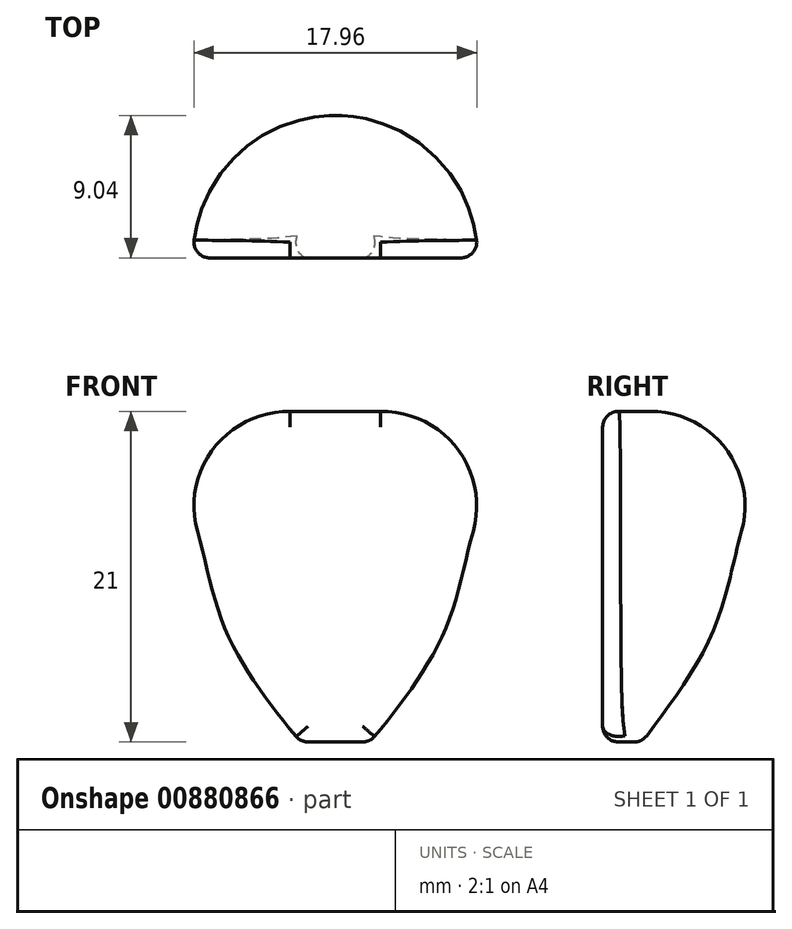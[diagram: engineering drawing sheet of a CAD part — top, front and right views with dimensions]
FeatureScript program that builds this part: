
annotation { "Feature Type Name" : "Feature", "Feature Type Description" : "" }
export const myFeature = defineFeature(function(context is Context, id is Id, definition is map)
    precondition{}
    {
        {
            var Q0;
            Q0=qCreatedBy(makeId("Top.planeOp"),FACE);
            cPlane(context, id + "F0", {"entities" : qUnion([Q0]), "cplaneType" : CPlaneType.OFFSET, "offset" : 10 * mm, "oppositeDirection" : true, "width" : 150 * mm, "height" : 150 * mm});
        }
        {
            var Q0;
            Q0=qCreatedBy(id+"F0.planeOp",FACE);
            cPlane(context, id + "F1", {"entities" : qUnion([Q0]), "cplaneType" : CPlaneType.OFFSET, "offset" : 10 * mm, "oppositeDirection" : true, "width" : 150 * mm, "height" : 150 * mm});
        }
        {
            var Q0;
            Q0=qCreatedBy(id+"F1.planeOp",FACE);
            cPlane(context, id + "F2", {"entities" : qUnion([Q0]), "cplaneType" : CPlaneType.OFFSET, "offset" : 7 * mm, "oppositeDirection" : true, "width" : 150 * mm, "height" : 150 * mm});
        }
        {
            var Q0;
            Q0=qCreatedBy(id+"F2.planeOp",FACE);
            cPlane(context, id + "F3", {"entities" : qUnion([Q0]), "cplaneType" : CPlaneType.OFFSET, "offset" : 7 * mm, "oppositeDirection" : true, "width" : 150 * mm, "height" : 150 * mm});
        }
        {
            var Q0;
            Q0=qCreatedBy(id+"F1.planeOp",FACE);
            var sketch = newSketch(context, id + "F4", { "sketchPlane" : qUnion([Q0])});
            skArc(sketch, "E0", {"start": v(12, 0) * mm, "mid": v(0, 12) * mm, "end": v(-12, 0) * mm});
            skLineSegment(sketch, "E1", {"start": v(-12, 0) * mm, "end": v(12, 0) * mm});
            skSolve(sketch);
        }
        {
            var Q0;
            Q0=qCreatedBy(id+"F3.planeOp",FACE);
            var sketch = newSketch(context, id + "F5", { "sketchPlane" : qUnion([Q0])});
            skArc(sketch, "E2", {"start": v(7, 0) * mm, "mid": v(0, 7) * mm, "end": v(-7, 0) * mm});
            skLineSegment(sketch, "E3", {"start": v(-7, 0) * mm, "end": v(7, 0) * mm});
            skSolve(sketch);
        }
        {
            var Q0;
            Q0=qCreatedBy(id+"F2.planeOp",FACE);
            var sketch = newSketch(context, id + "F6", { "sketchPlane" : qUnion([Q0])});
            skArc(sketch, "E4", {"start": v(9, 0) * mm, "mid": v(0, 9) * mm, "end": v(-9, 0) * mm});
            skLineSegment(sketch, "E5", {"start": v(-9, 0) * mm, "end": v(9, 0) * mm});
            skSolve(sketch);
        }
        {
            var Q0;
            Q0=qCreatedBy(id+"F3.planeOp",FACE);
            cPlane(context, id + "F7", {"entities" : qUnion([Q0]), "cplaneType" : CPlaneType.OFFSET, "offset" : 7 * mm, "oppositeDirection" : true, "width" : 150 * mm, "height" : 150 * mm});
        }
        {
            var Q0;
            Q0=qCreatedBy(id+"F7.planeOp",FACE);
            var sketch = newSketch(context, id + "F8", { "sketchPlane" : qUnion([Q0])});
            skArc(sketch, "E6", {"start": v(2.5, 0) * mm, "mid": v(0, 2.5) * mm, "end": v(-2.5, 0) * mm});
            skLineSegment(sketch, "E7", {"start": v(-2.5, 0) * mm, "end": v(2.5, 0) * mm});
            skSolve(sketch);
        }
        {
            var Q0;
            Q0=makeQuery(id+"F4.imprint","IMPRINT",FACE,{"disambiguationData":[TD([[makeQuery(id+"F4.imprint","IMPRINT",EDGE,{"derivedFrom":sQuery(id+"F4.wireOp",EDGE,"E0")}),1.0]])]});
            var Q1;
            Q1=makeQuery(id+"F6.imprint","IMPRINT",FACE,{"disambiguationData":[TD([[makeQuery(id+"F6.imprint","IMPRINT",EDGE,{"derivedFrom":sQuery(id+"F6.wireOp",EDGE,"E4")}),1.0]])]});
            var Q2;
            Q2=makeQuery(id+"F5.imprint","IMPRINT",FACE,{"disambiguationData":[TD([[makeQuery(id+"F5.imprint","IMPRINT",EDGE,{"derivedFrom":sQuery(id+"F5.wireOp",EDGE,"E2")}),1.0]])]});
            var Q3;
            Q3=makeQuery(id+"F8.imprint","IMPRINT",FACE,{"disambiguationData":[TD([[makeQuery(id+"F8.imprint","IMPRINT",EDGE,{"derivedFrom":sQuery(id+"F8.wireOp",EDGE,"E6")}),1.0]])]});
            loft(context, id + "F9", {"sheetProfilesArray" : [{ "sheetProfileEntities" : qUnion([Q0]) }, { "sheetProfileEntities" : qUnion([Q1]) }, { "sheetProfileEntities" : qUnion([Q2]) }, { "sheetProfileEntities" : qUnion([Q3]) }]});
        }
        {
            var Q0;
            {var subQ0=sQuery(id+"F4.wireOp",EDGE,"E0");var subQ1=sQuery(id+"F4.wireOp",EDGE,"E1");Q0=makeQuery(id+"F9.opLoft","MID_CAP_EDGE",EDGE,{"disambiguationData":[OSD([subQ0,subQ1]),TDD([makeQuery(id+"F4.imprint","INTERSECT",VERTEX,{"disambiguationData":[OD(0.0)],"derivedFrom":[subQ0,subQ1]}),makeQuery(id+"F4.imprint","INTERSECT",VERTEX,{"disambiguationData":[OD(1.0)],"derivedFrom":[subQ0,subQ1]}),makeQuery(id+"F4.imprint","IMPRINT",EDGE,{"derivedFrom":subQ0})])],"capPos":0.0});}
            fillet(context, id + "F10", {"entities" : qUnion([Q0]), "radius" : 6 * mm, "tangentPropagation" : true, "allowEdgeOverflow" : false});
        }
        {
            var Q0;
            {var subQ0=sQuery(id+"F8.wireOp",EDGE,"E7");var subQ1=sQuery(id+"F8.wireOp",EDGE,"E6");var subQ2=sQuery(id+"F6.wireOp",EDGE,"E5");var subQ3=sQuery(id+"F6.wireOp",EDGE,"E4");var subQ4=sQuery(id+"F5.wireOp",EDGE,"E3");var subQ5=sQuery(id+"F5.wireOp",EDGE,"E2");var subQ6=sQuery(id+"F4.wireOp",EDGE,"E1");var subQ7=sQuery(id+"F4.wireOp",EDGE,"E0");Q0=makeQuery(id+"F9.opLoft","SWEPT_EDGE",EDGE,{"disambiguationData":[OSD([subQ7,subQ6,subQ5,subQ4,subQ3,subQ2,subQ1,subQ0]),TDD([makeQuery(id+"F4.imprint","INTERSECT",VERTEX,{"disambiguationData":[OD(0.0)],"derivedFrom":[subQ7,subQ6]}),makeQuery(id+"F5.imprint","INTERSECT",VERTEX,{"disambiguationData":[OD(0.0)],"derivedFrom":[subQ5,subQ4]}),makeQuery(id+"F6.imprint","INTERSECT",VERTEX,{"disambiguationData":[OD(0.0)],"derivedFrom":[subQ3,subQ2]}),makeQuery(id+"F8.imprint","INTERSECT",VERTEX,{"disambiguationData":[OD(0.0)],"derivedFrom":[subQ1,subQ0]})])]});}
            fillet(context, id + "F11", {"entities" : qUnion([Q0]), "radius" : 1 * mm, "tangentPropagation" : true, "allowEdgeOverflow" : false});
        }
        {
            var Q0;
            {var subQ0=sQuery(id+"F8.wireOp",EDGE,"E6");var subQ1=sQuery(id+"F8.wireOp",EDGE,"E7");Q0=makeQuery(id+"F9.opLoft","MID_CAP_EDGE",EDGE,{"disambiguationData":[OSD([subQ0,subQ1]),TDD([makeQuery(id+"F8.imprint","INTERSECT",VERTEX,{"disambiguationData":[OD(0.0)],"derivedFrom":[subQ0,subQ1]}),makeQuery(id+"F8.imprint","INTERSECT",VERTEX,{"disambiguationData":[OD(1.0)],"derivedFrom":[subQ0,subQ1]}),makeQuery(id+"F8.imprint","IMPRINT",EDGE,{"derivedFrom":subQ0})])],"capPos":3.0});}
            fillet(context, id + "F12", {"entities" : qUnion([Q0]), "radius" : 1 * mm, "tangentPropagation" : true, "allowEdgeOverflow" : false});
        }
    });
